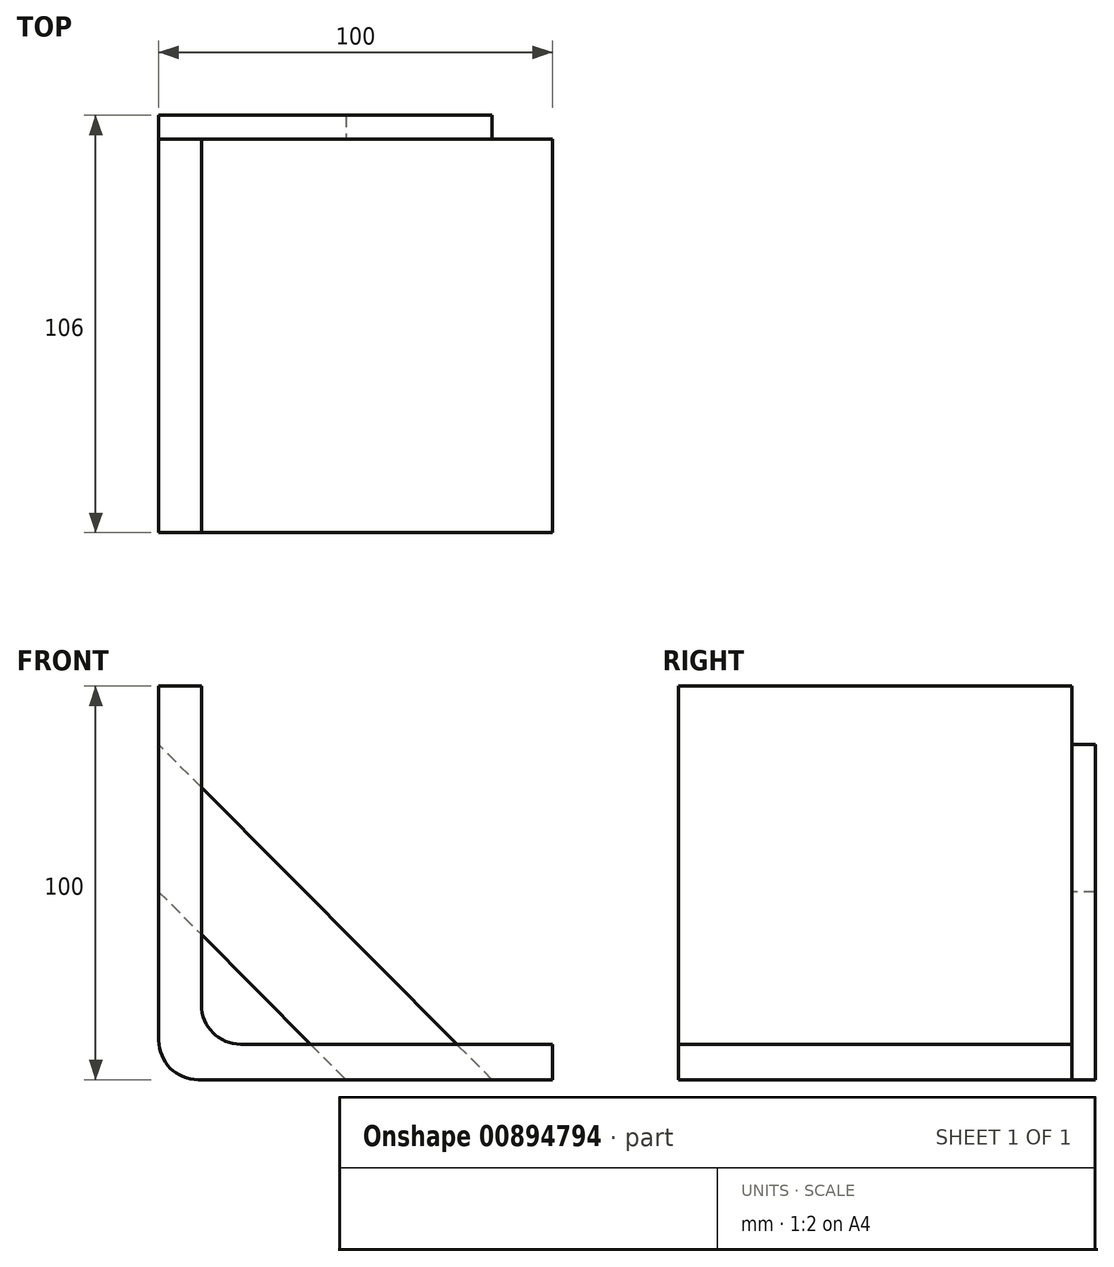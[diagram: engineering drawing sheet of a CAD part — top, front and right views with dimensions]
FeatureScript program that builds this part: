
annotation { "Feature Type Name" : "Feature", "Feature Type Description" : "" }
export const myFeature = defineFeature(function(context is Context, id is Id, definition is map)
    precondition{}
    {
        {
            var Q0;
            Q0=qCreatedBy(makeId("Front.planeOp"),FACE);
            var sketch = newSketch(context, id + "F0", { "sketchPlane" : qUnion([Q0])});
            skLineSegment(sketch, "E0", {"start": v(0, 100) * mm, "end": v(0, 10) * mm});
            skLineSegment(sketch, "E1", {"start": v(10, 0) * mm, "end": v(100, 0) * mm});
            skLineSegment(sketch, "E2", {"start": v(100, 0) * mm, "end": v(100, 8.98) * mm});
            skLineSegment(sketch, "E3", {"start": v(100, 8.98) * mm, "end": v(20.82, 8.98) * mm});
            skLineSegment(sketch, "E4", {"start": v(10.82, 18.98) * mm, "end": v(10.82, 100) * mm});
            skLineSegment(sketch, "E5", {"start": v(10.82, 100) * mm, "end": v(0, 100) * mm});
            skPoint(sketch, "E6.visualSharp", {"position": v(0, 0) * mm});
            skArc(sketch, "E6.filletArc", {"start": v(0, 10) * mm, "mid": v(2.93, 2.93) * mm, "end": v(10, 0) * mm});
            skPoint(sketch, "E7.visualSharp", {"position": v(10.82, 8.98) * mm});
            skArc(sketch, "E7.filletArc", {"start": v(10.82, 18.98) * mm, "mid": v(13.75, 11.91) * mm, "end": v(20.82, 8.98) * mm});
            skSolve(sketch);
        }
        {
            var Q0;
            Q0=makeQuery(id+"F0.imprint","IMPRINT",FACE,{"disambiguationData":[TD([[makeQuery(id+"F0.imprint","IMPRINT",EDGE,{"derivedFrom":sQuery(id+"F0.wireOp",EDGE,"E0")}),1.0]])]});
            extrude(context, id + "F1", {"entities" : qUnion([Q0]), "depth" : 100 * mm, "offsetDistance" : 25 * mm});
        }
        {
            var Q0;
            Q0=qCreatedBy(makeId("Front.planeOp"),FACE);
            var sketch = newSketch(context, id + "F2", { "sketchPlane" : qUnion([Q0])});
            skLineSegment(sketch, "E8", {"start": v(84.68, 0) * mm, "end": v(0, 85.1) * mm});
            skLineSegment(sketch, "E9", {"start": v(0, 85.1) * mm, "end": v(0, 47.76) * mm});
            skLineSegment(sketch, "E10", {"start": v(0, 47.76) * mm, "end": v(47.52, 0) * mm});
            skLineSegment(sketch, "E11", {"start": v(47.52, 0) * mm, "end": v(84.68, 0) * mm});
            skSolve(sketch);
        }
        {
            var Q0;
            Q0 = qSketchRegion(id + "F2", true);
            extrude(context, id + "F3", {"entities" : qUnion([Q0]), "operationType" : NewBodyOperationType.ADD, "oppositeDirection" : true, "depth" : 6 * mm, "offsetDistance" : 25 * mm});
        }
    });
